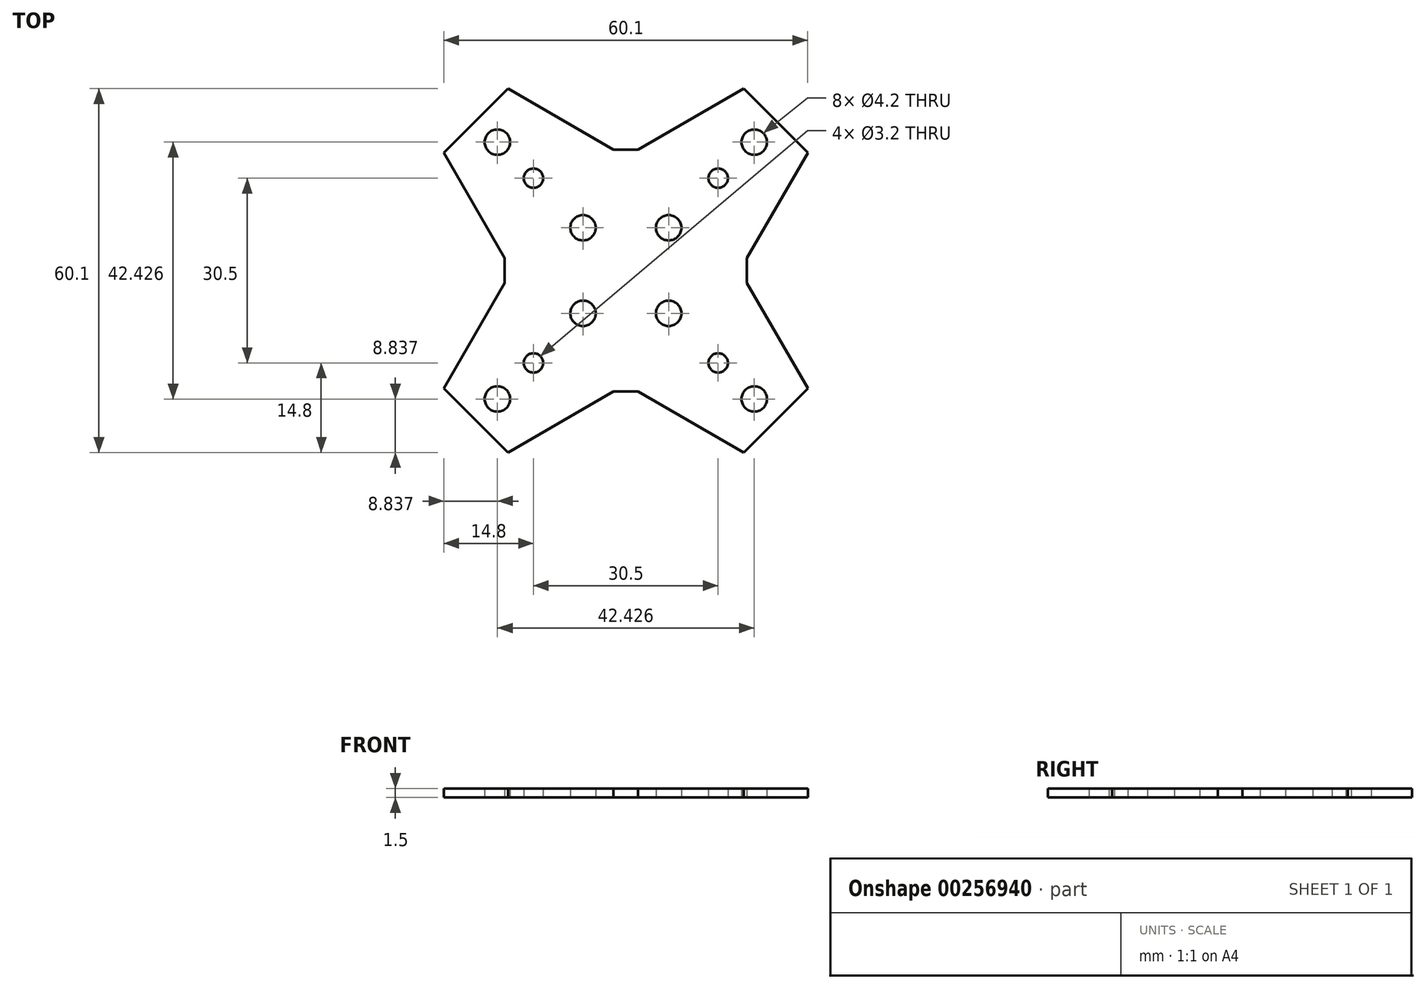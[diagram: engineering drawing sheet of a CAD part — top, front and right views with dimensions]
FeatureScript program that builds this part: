
annotation { "Feature Type Name" : "Feature", "Feature Type Description" : "" }
export const myFeature = defineFeature(function(context is Context, id is Id, definition is map)
    precondition{}
    {
        {
            var Q0;
            Q0=qCreatedBy(makeId("Top.planeOp"),FACE);
            var sketch = newSketch(context, id + "F0", { "sketchPlane" : qUnion([Q0])});
            skLineSegment(sketch, "E0", {"start": v(-30.05, 19.45) * mm, "end": v(-19.45, 30.05) * mm});
            skLineSegment(sketch, "E1", {"start": v(-2.03, 20) * mm, "end": v(2.03, 20) * mm});
            skLineSegment(sketch, "E2", {"start": v(-19.45, 30.05) * mm, "end": v(-2.03, 20) * mm});
            skLineSegment(sketch, "E3.1.0", {"start": v(-20, -2.03) * mm, "end": v(-20, 2.03) * mm});
            skLineSegment(sketch, "E3.1.1", {"start": v(-19.45, -30.05) * mm, "end": v(-30.05, -19.45) * mm});
            skLineSegment(sketch, "E3.1.2", {"start": v(-30.05, -19.45) * mm, "end": v(-20, -2.03) * mm});
            skLineSegment(sketch, "E3.2.0", {"start": v(2.03, -20) * mm, "end": v(-2.03, -20) * mm});
            skLineSegment(sketch, "E3.2.1", {"start": v(30.05, -19.45) * mm, "end": v(19.45, -30.05) * mm});
            skLineSegment(sketch, "E3.2.2", {"start": v(19.45, -30.05) * mm, "end": v(2.03, -20) * mm});
            skLineSegment(sketch, "E3.3.0", {"start": v(20, 2.03) * mm, "end": v(20, -2.03) * mm});
            skLineSegment(sketch, "E3.3.1", {"start": v(19.45, 30.05) * mm, "end": v(30.05, 19.45) * mm});
            skLineSegment(sketch, "E3.3.2", {"start": v(30.05, 19.45) * mm, "end": v(20, 2.03) * mm});
            skPoint(sketch, "E3.center", {"position": v(0, 0) * mm});
            skLineSegment(sketch, "E4", {"start": v(-30.05, 19.45) * mm, "end": v(-20, 2.03) * mm});
            skLineSegment(sketch, "E5", {"start": v(19.45, 30.05) * mm, "end": v(2.03, 20) * mm});
            skLineSegment(sketch, "E6", {"start": v(-19.45, -30.05) * mm, "end": v(-2.03, -20) * mm});
            skLineSegment(sketch, "E7", {"start": v(30.05, -19.45) * mm, "end": v(20, -2.03) * mm});
            skLineSegment(sketch, "E8", {"start": v(0, 0) * mm, "end": v(-24.75, 24.75) * mm, "construction": true});
            skCircle(sketch, "E9", {"center": v(-21.21, 21.21) * mm, "radius": 2.1 * mm});
            skCircle(sketch, "E10", {"center": v(-7.07, 7.07) * mm, "radius": 2.1 * mm});
            skCircle(sketch, "E11", {"center": v(-15.25, 15.25) * mm, "radius": 1.6 * mm});
            skCircle(sketch, "E12.1.0", {"center": v(-7.07, -7.07) * mm, "radius": 2.1 * mm});
            skCircle(sketch, "E12.1.1", {"center": v(-15.25, -15.25) * mm, "radius": 1.6 * mm});
            skCircle(sketch, "E12.1.2", {"center": v(-21.21, -21.21) * mm, "radius": 2.1 * mm});
            skCircle(sketch, "E12.2.0", {"center": v(7.07, -7.07) * mm, "radius": 2.1 * mm});
            skCircle(sketch, "E12.2.1", {"center": v(15.25, -15.25) * mm, "radius": 1.6 * mm});
            skCircle(sketch, "E12.2.2", {"center": v(21.21, -21.21) * mm, "radius": 2.1 * mm});
            skCircle(sketch, "E13.1.3.0", {"center": v(7.07, 7.07) * mm, "radius": 2.1 * mm});
            skCircle(sketch, "E13.2.3.0", {"center": v(15.25, 15.25) * mm, "radius": 1.6 * mm});
            skCircle(sketch, "E13.4.3.0", {"center": v(21.21, 21.21) * mm, "radius": 2.1 * mm});
            skSolve(sketch);
        }
        {
            var Q0;
            Q0 = qSketchRegion(id + "F0", true);
            extrude(context, id + "F1", {"entities" : qUnion([Q0]), "depth" : 1.5 * mm});
        }
    });
